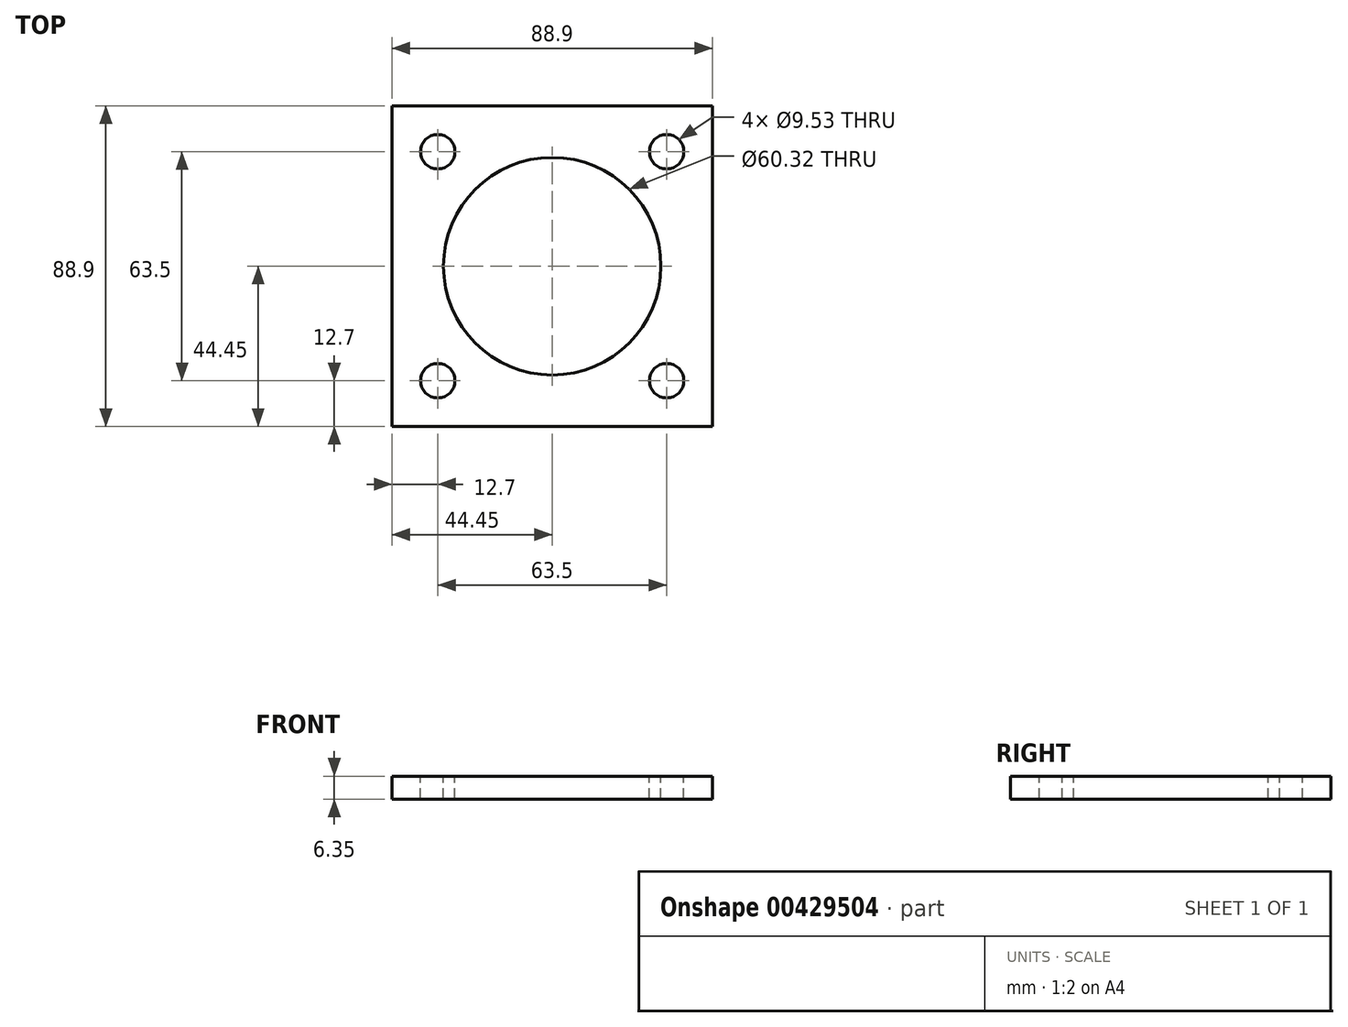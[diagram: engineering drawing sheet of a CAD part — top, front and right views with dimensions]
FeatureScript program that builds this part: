
annotation { "Feature Type Name" : "Feature", "Feature Type Description" : "" }
export const myFeature = defineFeature(function(context is Context, id is Id, definition is map)
    precondition{}
    {
        {
            var Q0;
            Q0=qCreatedBy(makeId("Top.planeOp"),FACE);
            var sketch = newSketch(context, id + "F0", { "sketchPlane" : qUnion([Q0])});
            skLineSegment(sketch, "E0.bottom", {"start": v(44.45, 44.45) * mm, "end": v(-44.45, 44.45) * mm});
            skLineSegment(sketch, "E0.top", {"start": v(44.45, -44.45) * mm, "end": v(-44.45, -44.45) * mm});
            skLineSegment(sketch, "E0.left", {"start": v(44.45, 44.45) * mm, "end": v(44.45, -44.45) * mm});
            skLineSegment(sketch, "E0.right", {"start": v(-44.45, 44.45) * mm, "end": v(-44.45, -44.45) * mm});
            skPoint(sketch, "E0.middle", {"position": v(0, 0) * mm});
            skCircle(sketch, "E1", {"center": v(0, 0) * mm, "radius": 30.16 * mm});
            skCircle(sketch, "E2", {"center": v(-31.75, 31.75) * mm, "radius": 4.76 * mm});
            skCircle(sketch, "E3.0.1.0", {"center": v(-31.75, -31.75) * mm, "radius": 4.76 * mm});
            skCircle(sketch, "E3.1.0.0", {"center": v(31.75, 31.75) * mm, "radius": 4.76 * mm});
            skCircle(sketch, "E3.1.1.0", {"center": v(31.75, -31.75) * mm, "radius": 4.76 * mm});
            skLineSegment(sketch, "E3.direction1", {"start": v(-31.75, 31.75) * mm, "end": v(31.75, 31.75) * mm, "construction": true});
            skLineSegment(sketch, "E3.direction2", {"start": v(-31.75, 31.75) * mm, "end": v(-31.75, -31.75) * mm, "construction": true});
            skSolve(sketch);
        }
        {
            var Q0;
            Q0 = qSketchRegion(id + "F0", true);
            extrude(context, id + "F1", {"entities" : qUnion([Q0]), "oppositeDirection" : true, "depth" : 6.35 * mm});
        }
    });
